# Revit family: Copper flat patch panels equipped
name_source: partatom
category: Equipement spécialisé
units: mm (PartAtom-declared; Revit-internal decimal feet)

## family parameters
Basée sur le plan de construction = Non
Cote de connecteur circulaire = Utiliser le diamètre
Couper avec des vides une fois chargée = Non
Partagée = Oui
Point de calcul de pièce = Non
Toujours verticalement = Oui
Type d'élément = Normal

## types (8) — shared parameters
Application class = EC001128
Cable nature for connection = Flexible or rigid
Cable support = With zigzag
Color = IDS_NOIR
Connection type = Insulation displacement connector
Connector type = RJ45
Degree of protection IK = IK03
E-catalogue link = https://www.legrand.fr
Function = Flat patch panels equipped
Modular spacing = 19 inches
Number of connectors = 24
Number of height units = 1
Operating temperature = -25°C à 70°C
RAL Number = 9017
Storage temperature = -40°C à 70°C
zero-valued in all types: Elévation par défaut

## per-type parameters (varying)
| type | Category | Depth | EAN | Height | Legrand part number | Shielded | Width (mm) |
| Flat patch panel 24 RJ45 Cat 5e UTP 1U | 5E | 321.7 mm | 3414970870308 | 43.85 mm  [stored 0.143865 ft] | 033750 | Non | 482.5 mm |
| Flat patch panel 24 RJ45 Cat 5e FTP 1U | 5E | 321.7 mm | 3414970870322 | 43.85 mm  [stored 0.143865 ft] | 033751 | Oui | 482.5 mm |
| Flat patch panel 24 RJ45 Cat 6 UTP 1U | 6 | 321.7 mm | 3414970870537 | 43.85 mm  [stored 0.143865 ft] | 033760 | Non | 482.5 mm |
| Flat patch panel 24 RJ45 Cat 6 FTP 1U | 6 | 321.7 mm | 3414970870551 | 43.85 mm  [stored 0.143865 ft] | 033761 | Oui | 482.5 mm |
| Flat patch panel 24 RJ45 Cat 6 STP 1U | 6 | 321.7 mm | 3414970870575 | 43.85 mm  [stored 0.143865 ft] | 033762 | Oui | 482.5 mm |
| Flat patch panel 24 RJ45 Cat 6A UTP 1U | 6A | 321.7 mm | 3414970870681 | 43.85 mm  [stored 0.143865 ft] | 033770 | Non | 482.5 mm |
| Flat patch panel 24 RJ45 Cat 6A STP 1U | 6A | 321.7 mm | 3414970870704 | 43.85 mm  [stored 0.143865 ft] | 033772 | Oui | 482.5 mm |
| Flat patch panel 24 RJ45 Cat 8 STP 1U | 8 | 120 mm | 3414970982063 | 44.45 mm | 033782 | Oui | 482.6 mm |

note: column(s) folded — value = type name in every type: BIM wording

note: [stored X ft] marks values corroborated as IEEE doubles in the binary element streams (Revit-internal decimal feet)
